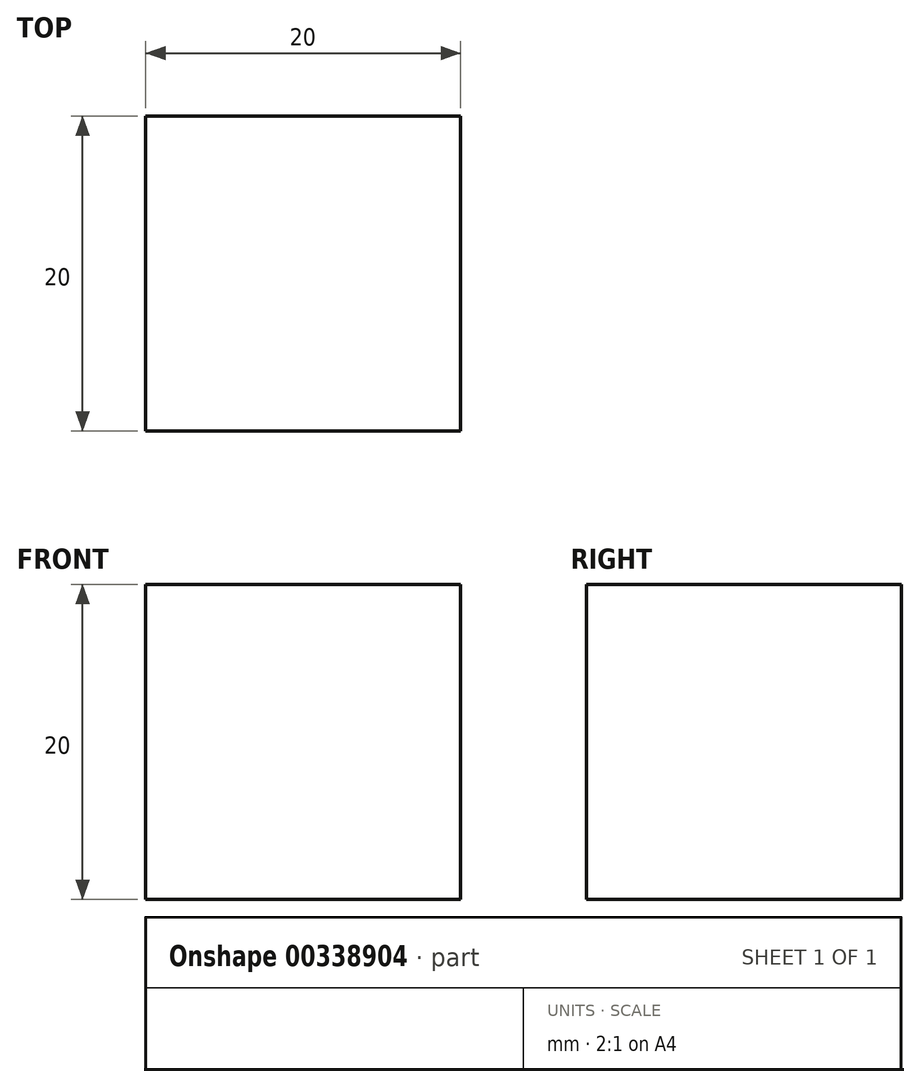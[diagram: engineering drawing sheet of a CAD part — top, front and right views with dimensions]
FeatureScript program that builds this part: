
annotation { "Feature Type Name" : "Feature", "Feature Type Description" : "" }
export const myFeature = defineFeature(function(context is Context, id is Id, definition is map)
    precondition{}
    {
        {
            var Q0;
            Q0=qCreatedBy(makeId("Top.planeOp"),FACE);
            var sketch = newSketch(context, id + "F0", { "sketchPlane" : qUnion([Q0])});
            skLineSegment(sketch, "E0.bottom", {"start": v(0, 0) * mm, "end": v(20, 0) * mm});
            skLineSegment(sketch, "E0.top", {"start": v(0, -20) * mm, "end": v(20, -20) * mm});
            skLineSegment(sketch, "E0.left", {"start": v(0, 0) * mm, "end": v(0, -20) * mm});
            skLineSegment(sketch, "E0.right", {"start": v(20, 0) * mm, "end": v(20, -20) * mm});
            skSolve(sketch);
        }
        {
            var Q0;
            Q0 = qSketchRegion(id + "F0", true);
            extrude(context, id + "F1", {"entities" : qUnion([Q0]), "depth" : 20 * mm});
        }
    });
